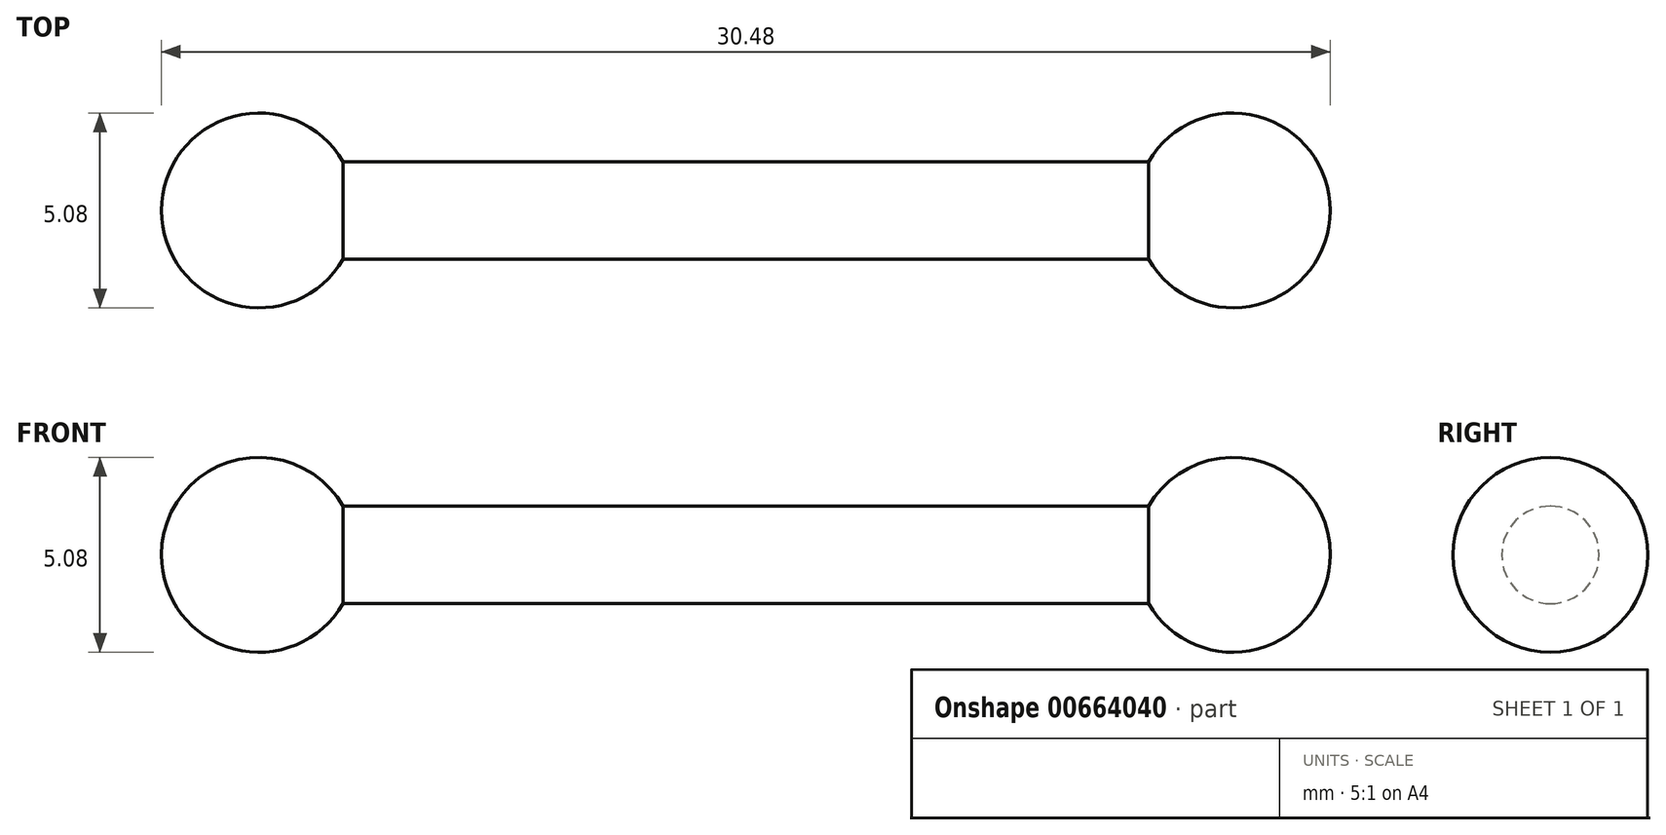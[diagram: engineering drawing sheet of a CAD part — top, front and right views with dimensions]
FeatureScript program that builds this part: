
annotation { "Feature Type Name" : "Feature", "Feature Type Description" : "" }
export const myFeature = defineFeature(function(context is Context, id is Id, definition is map)
    precondition{}
    {
        {
            var Q0;
            Q0=qCreatedBy(makeId("Front.planeOp"),FACE);
            var sketch = newSketch(context, id + "F0", { "sketchPlane" : qUnion([Q0])});
            skArc(sketch, "E0", {"start": v(23.24, 0) * mm, "mid": v(21.36, 2.45) * mm, "end": v(18.5, 1.27) * mm});
            skLineSegment(sketch, "E1.bottom", {"start": v(20.7, 0) * mm, "end": v(-4.7, 0) * mm});
            skLineSegment(sketch, "E1.top", {"start": v(18.5, 1.27) * mm, "end": v(-2.5, 1.27) * mm});
            skLineSegment(sketch, "E2", {"start": v(20.7, 0) * mm, "end": v(23.24, 0) * mm});
            skPoint(sketch, "E3", {"position": v(8, 1.27) * mm});
            skArc(sketch, "E4.MirrorCS", {"start": v(-7.24, 0) * mm, "mid": v(-5.36, 2.45) * mm, "end": v(-2.5, 1.27) * mm});
            skLineSegment(sketch, "E5.MirrorCS", {"start": v(-4.7, 0) * mm, "end": v(-7.24, 0) * mm});
            skPoint(sketch, "E6.end.orphan", {"position": v(8, 2.83) * mm});
            skPoint(sketch, "E7.orphan", {"position": v(-4.7, 1.27) * mm});
            skPoint(sketch, "E1.left.end.orphan", {"position": v(20.7, 1.27) * mm});
            skPoint(sketch, "E8.end.orphan", {"position": v(8, 0) * mm});
            skSolve(sketch);
        }
        {
            var Q0;
            Q0=makeQuery(id+"F0.imprint","IMPRINT",FACE,{"disambiguationData":[TD([[makeQuery(id+"F0.imprint","IMPRINT",EDGE,{"derivedFrom":sQuery(id+"F0.wireOp",EDGE,"E0")}),1.0]])]});
            var Q1;
            Q1=sQuery(id+"F0.wireOp",EDGE,"E1.bottom");
            revolve(context, id + "F1", {"entities" : qUnion([Q0]), "axis" : qUnion([Q1]), "revolveType" : RevolveType.FULL});
        }
    });
